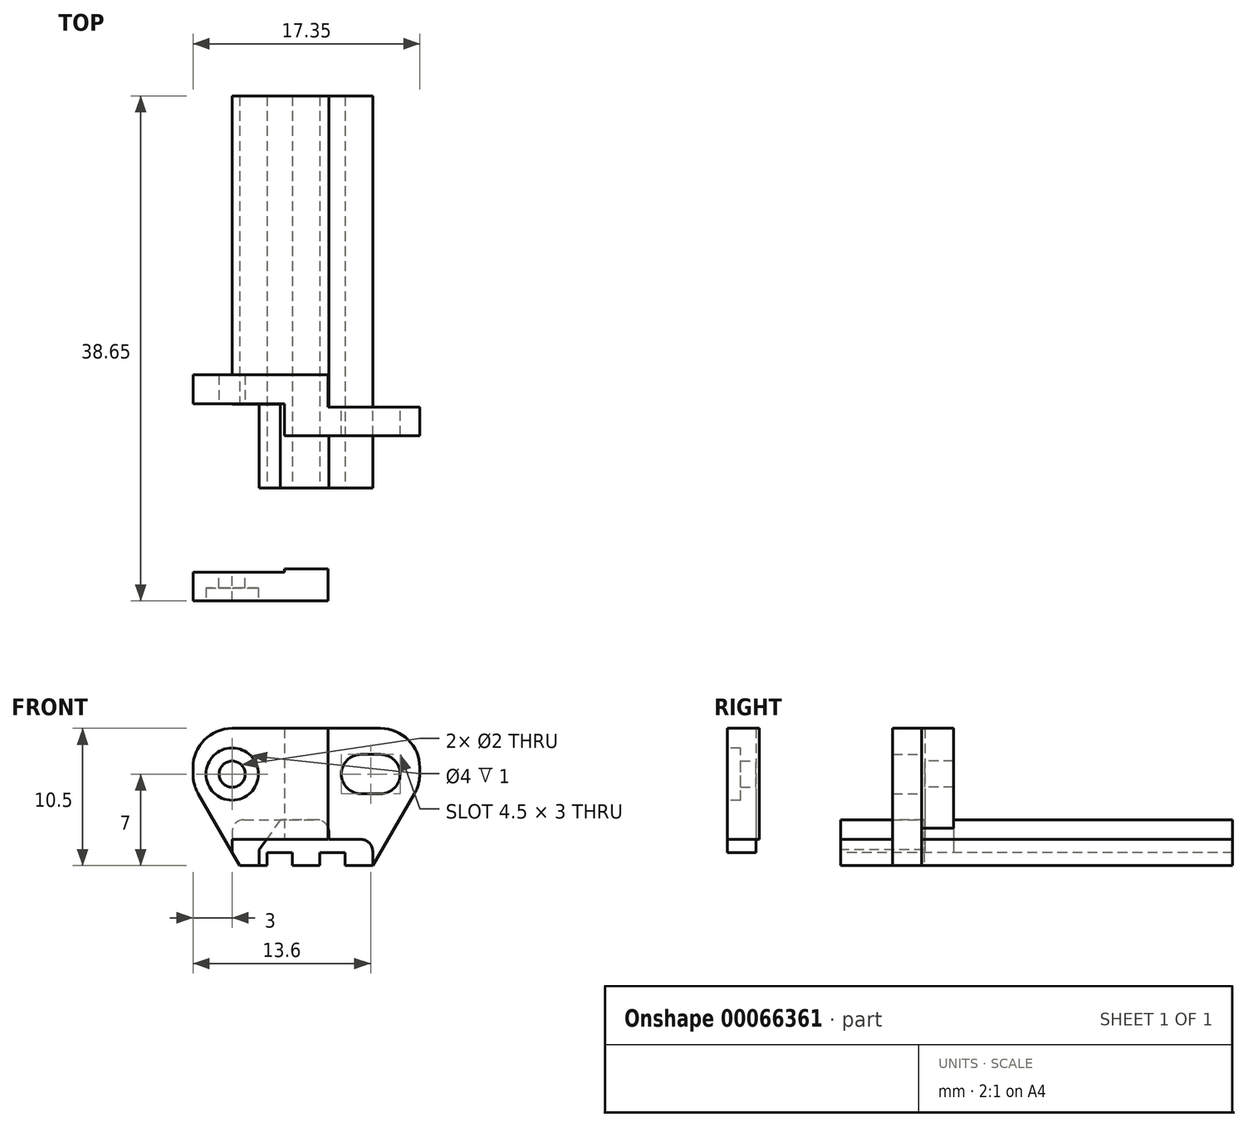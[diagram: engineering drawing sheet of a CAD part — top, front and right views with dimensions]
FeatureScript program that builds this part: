
annotation { "Feature Type Name" : "Feature", "Feature Type Description" : "" }
export const myFeature = defineFeature(function(context is Context, id is Id, definition is map)
    precondition{}
    {
        {
            var Q0;
            Q0=qCreatedBy(makeId("Front.planeOp"),FACE);
            var sketch = newSketch(context, id + "F0", { "sketchPlane" : qUnion([Q0])});
            skLineSegment(sketch, "E0", {"start": v(-8, 5) * mm, "end": v(24.45, 5) * mm, "construction": true});
            skArc(sketch, "E1", {"start": v(11.35, 3.5) * mm, "mid": v(12.85, 5) * mm, "end": v(11.35, 6.5) * mm});
            skArc(sketch, "E2", {"start": v(-3, 5) * mm, "mid": v(-2.65, 3.6) * mm, "end": v(-1.7, 2.52) * mm});
            skArc(sketch, "E3", {"start": v(14.35, 5) * mm, "mid": v(14, 3.6) * mm, "end": v(13.04, 2.52) * mm});
            skLineSegment(sketch, "E4", {"start": v(-1.7, 2.52) * mm, "end": v(2, 0) * mm});
            skLineSegment(sketch, "E5", {"start": v(13.04, 2.52) * mm, "end": v(9.35, 0) * mm});
            skLineSegment(sketch, "E6", {"start": v(4, 8.5) * mm, "end": v(4, 2) * mm});
            skLineSegment(sketch, "E7", {"start": v(9.35, 2) * mm, "end": v(7.35, 2) * mm});
            skLineSegment(sketch, "E8", {"start": v(4, 2) * mm, "end": v(2, 2) * mm});
            skLineSegment(sketch, "E9", {"start": v(4, 2) * mm, "end": v(7.35, 2) * mm});
            skLineSegment(sketch, "E10", {"start": v(7.35, 8.5) * mm, "end": v(7.35, 2) * mm});
            skLineSegment(sketch, "E11", {"start": v(2, 0) * mm, "end": v(9.35, 0) * mm});
            skLineSegment(sketch, "E12", {"start": v(2, 0) * mm, "end": v(2, 2) * mm});
            skLineSegment(sketch, "E13", {"start": v(9.35, 0) * mm, "end": v(9.35, 2) * mm});
            skLineSegment(sketch, "E14", {"start": v(0, 8.5) * mm, "end": v(11.35, 8.5) * mm});
            skLineSegment(sketch, "E15", {"start": v(-3, 5) * mm, "end": v(-3, 5.5) * mm});
            skLineSegment(sketch, "E16", {"start": v(14.35, 5) * mm, "end": v(14.35, 5.5) * mm});
            skPoint(sketch, "E16.endSnap0", {"position": v(14.35, 5) * mm});
            skPoint(sketch, "E17.visualSharp", {"position": v(-3, 8.5) * mm});
            skArc(sketch, "E17.filletArc", {"start": v(0, 8.5) * mm, "mid": v(-2.12, 7.62) * mm, "end": v(-3, 5.5) * mm});
            skPoint(sketch, "E18.visualSharp", {"position": v(14.35, 8.5) * mm});
            skArc(sketch, "E18.filletArc", {"start": v(14.35, 5.5) * mm, "mid": v(13.47, 7.62) * mm, "end": v(11.35, 8.5) * mm});
            skArc(sketch, "E19", {"start": v(9.85, 6.5) * mm, "mid": v(8.35, 5) * mm, "end": v(9.85, 3.5) * mm});
            skLineSegment(sketch, "E20", {"start": v(9.85, 6.5) * mm, "end": v(11.35, 6.5) * mm});
            skLineSegment(sketch, "E21", {"start": v(9.85, 3.5) * mm, "end": v(11.35, 3.5) * mm});
            skCircle(sketch, "E22", {"center": v(0, 5) * mm, "radius": 1 * mm});
            skSolve(sketch);
        }
        {
            var Q0;
            Q0=qCreatedBy(makeId("Front.planeOp"),FACE);
            var sketch = newSketch(context, id + "F1", { "sketchPlane" : qUnion([Q0])});
            skLineSegment(sketch, "E23.0", {"start": v(7.35, 8.5) * mm, "end": v(7.35, 2) * mm});
            skPoint(sketch, "E24.0.start.orphan", {"position": v(4, 2) * mm});
            skPoint(sketch, "E25.0.start.orphan", {"position": v(2, 0) * mm});
            skLineSegment(sketch, "E26.0", {"start": v(0, 8.5) * mm, "end": v(7.35, 8.5) * mm});
            skArc(sketch, "E27.0", {"start": v(0, 8.5) * mm, "mid": v(-2.12, 7.62) * mm, "end": v(-3, 5.5) * mm});
            skPoint(sketch, "E28.0", {"position": v(7.35, 0) * mm});
            skLineSegment(sketch, "E29.0", {"start": v(7.35, 2) * mm, "end": v(7.35, 0) * mm});
            skPoint(sketch, "E30.0.2.end.orphan", {"position": v(9.35, 2) * mm});
            skPoint(sketch, "E31.orphan", {"position": v(9.35, 0) * mm});
            skPoint(sketch, "E32.orphan", {"position": v(11.35, 8.5) * mm});
            skLineSegment(sketch, "E33", {"start": v(0, 0) * mm, "end": v(2, 0) * mm});
            skLineSegment(sketch, "E34", {"start": v(2, 0) * mm, "end": v(7.35, 0) * mm});
            skPoint(sketch, "E35.0.end.orphan", {"position": v(-3, 8.2) * mm});
            skLineSegment(sketch, "E36", {"start": v(-3, 4) * mm, "end": v(-3, 5.5) * mm});
            skArc(sketch, "E37.0", {"start": v(-3, 5) * mm, "mid": v(-2.9, 4.22) * mm, "end": v(-2.6, 3.5) * mm});
            skLineSegment(sketch, "E38", {"start": v(-2.6, 3.5) * mm, "end": v(-0.58, 0) * mm});
            skPoint(sketch, "E39.orphan", {"position": v(-1.7, 2.52) * mm});
            skLineSegment(sketch, "E40", {"start": v(0, 0) * mm, "end": v(0, -1) * mm});
            skLineSegment(sketch, "E41", {"start": v(0, -1) * mm, "end": v(-0.58, 0) * mm});
            skCircle(sketch, "E42.0", {"center": v(0, 5) * mm, "radius": 1 * mm});
            skSolve(sketch);
        }
        {
            var Q0;
            Q0=qSketchRegion(id+"F1",true);
            var Q1;
            Q1 = qSketchRegion(id + "F8", true);
            extrude(context, id + "F2", {"entities" : qUnion([Q0, Q1]), "oppositeDirection" : true, "depth" : 2.2 * mm});
        }
        {
            var Q0;
            Q0=qCreatedBy(makeId("Front.planeOp"),FACE);
            var sketch = newSketch(context, id + "F3", { "sketchPlane" : qUnion([Q0])});
            skLineSegment(sketch, "E43.0", {"start": v(4, 8.5) * mm, "end": v(4, 2) * mm});
            skLineSegment(sketch, "E44.0", {"start": v(7.35, 8.5) * mm, "end": v(7.35, 2) * mm});
            skLineSegment(sketch, "E45.0", {"start": v(4, 8.5) * mm, "end": v(7.35, 8.5) * mm});
            skLineSegment(sketch, "E46", {"start": v(7.35, 2) * mm, "end": v(7.35, 0) * mm});
            skLineSegment(sketch, "E47", {"start": v(7.35, 0) * mm, "end": v(4, 0) * mm});
            skLineSegment(sketch, "E48", {"start": v(4, 0) * mm, "end": v(4, 2) * mm});
            skPoint(sketch, "E49.0", {"position": v(7.35, 0) * mm});
            skPoint(sketch, "E50.0", {"position": v(4, 8.5) * mm});
            skPoint(sketch, "E51.0", {"position": v(7.35, 8.5) * mm});
            skPoint(sketch, "E52.0", {"position": v(4, 0) * mm});
            skSolve(sketch);
        }
        {
            var Q0;
            Q0=makeQuery(id+"F3.imprint","IMPRINT",FACE,{"disambiguationData":[TD([[makeQuery(id+"F3.imprint","IMPRINT",EDGE,{"derivedFrom":sQuery(id+"F3.wireOp",EDGE,"E43.0")}),1.0]])]});
            extrude(context, id + "F4", {"entities" : qUnion([Q0]), "operationType" : NewBodyOperationType.ADD, "depth" : .25 * mm});
        }
        {
            var Q0;
            Q0=makeQuery(id+"F4.opExtrude","CAP_FACE",FACE,{"disambiguationData":[OSD([sQuery(id+"F3.wireOp",EDGE,"E43.0"),sQuery(id+"F3.wireOp",EDGE,"E44.0"),sQuery(id+"F3.wireOp",EDGE,"E45.0"),sQuery(id+"F3.wireOp",EDGE,"E46"),sQuery(id+"F3.wireOp",EDGE,"E47"),sQuery(id+"F3.wireOp",EDGE,"E48")])],"isStart":false});
            var sketch = newSketch(context, id + "F5", { "sketchPlane" : qUnion([Q0])});
            skArc(sketch, "E53.0", {"start": v(14.35, 5) * mm, "mid": v(14.25, 4.22) * mm, "end": v(13.94, 3.5) * mm});
            skLineSegment(sketch, "E54", {"start": v(10.75, -1) * mm, "end": v(10.75, -2) * mm});
            skLineSegment(sketch, "E55", {"start": v(10.75, -2) * mm, "end": v(13.94, 3.5) * mm});
            skLineSegment(sketch, "E56.0", {"start": v(4, 8.5) * mm, "end": v(4, 2) * mm});
            skArc(sketch, "E57.0", {"start": v(14.35, 5.5) * mm, "mid": v(13.47, 7.62) * mm, "end": v(11.35, 8.5) * mm});
            skLineSegment(sketch, "E58.0", {"start": v(14.35, 5) * mm, "end": v(14.35, 5.5) * mm});
            skLineSegment(sketch, "E59", {"start": v(4, 2) * mm, "end": v(4, 0) * mm});
            skPoint(sketch, "E60.orphan", {"position": v(2, 0) * mm});
            skLineSegment(sketch, "E61.trimOffspring", {"start": v(4, 8.5) * mm, "end": v(11.35, 8.5) * mm});
            skPoint(sketch, "E62.0.start.orphan", {"position": v(0, 8.5) * mm});
            skLineSegment(sketch, "E63", {"start": v(7.39, 0) * mm, "end": v(10.75, -1) * mm});
            skLineSegment(sketch, "E64", {"start": v(4, 0) * mm, "end": v(7.39, 0) * mm});
            skLineSegment(sketch, "E65.0", {"start": v(9.85, 3.5) * mm, "end": v(11.35, 3.5) * mm});
            skArc(sketch, "E66.0", {"start": v(9.85, 6.5) * mm, "mid": v(8.35, 5) * mm, "end": v(9.85, 3.5) * mm});
            skLineSegment(sketch, "E67.0", {"start": v(9.85, 6.5) * mm, "end": v(11.35, 6.5) * mm});
            skArc(sketch, "E68.0", {"start": v(11.35, 3.5) * mm, "mid": v(12.85, 5) * mm, "end": v(11.35, 6.5) * mm});
            skSolve(sketch);
        }
        {
            var Q0;
            Q0=qSketchRegion(id+"F5",true);
            extrude(context, id + "F6", {"entities" : qUnion([Q0]), "depth" : 2.2 * mm});
        }
        {
            var Q0;
            Q0=makeQuery(id+"F6.opExtrude","CAP_FACE",FACE,{"disambiguationData":[OSD([sQuery(id+"F5.wireOp",EDGE,"E53.0"),sQuery(id+"F5.wireOp",EDGE,"234c2655-9adb-407f-9d6a-58d03281b655.0"),sQuery(id+"F5.wireOp",EDGE,"E54"),sQuery(id+"F5.wireOp",EDGE,"E55"),sQuery(id+"F5.wireOp",EDGE,"E56.0"),sQuery(id+"F5.wireOp",EDGE,"E57.0"),sQuery(id+"F5.wireOp",EDGE,"E58.0"),sQuery(id+"F5.wireOp",EDGE,"E59"),sQuery(id+"F5.wireOp",EDGE,"E61.trimOffspring"),sQuery(id+"F5.wireOp",EDGE,"E63"),sQuery(id+"F5.wireOp",EDGE,"E64")])],"isStart":false});
            cPlane(context, id + "F7", {"entities" : qUnion([Q0]), "cplaneType" : CPlaneType.OFFSET, "offset" : 4 * mm, "width" : 150 * mm, "height" : 150 * mm});
        }
        {
            var Q0;
            Q0=qCreatedBy(id+"F7.planeOp",FACE);
            var sketch = newSketch(context, id + "F8", { "sketchPlane" : qUnion([Q0])});
            skLineSegment(sketch, "E69.0", {"start": v(10.75, -2) * mm, "end": v(13.94, 3.5) * mm});
            skLineSegment(sketch, "E70.0", {"start": v(10.75, -1) * mm, "end": v(10.75, -2) * mm});
            skLineSegment(sketch, "E71", {"start": v(7.39, 0) * mm, "end": v(7.39, 0) * mm});
            skLineSegment(sketch, "E72", {"start": v(7.39, 0) * mm, "end": v(7.39, 0.6) * mm});
            skLineSegment(sketch, "E73", {"start": v(6.49, 1.5) * mm, "end": v(0.9, 1.5) * mm});
            skLineSegment(sketch, "E74", {"start": v(10.75, -2) * mm, "end": v(8.65, -2) * mm});
            skLineSegment(sketch, "E75", {"start": v(8.65, -2) * mm, "end": v(8.65, -1) * mm});
            skLineSegment(sketch, "E76", {"start": v(8.65, -1) * mm, "end": v(6.71, -1) * mm});
            skLineSegment(sketch, "E77", {"start": v(6.71, -1) * mm, "end": v(6.71, -2) * mm});
            skLineSegment(sketch, "E78", {"start": v(6.71, -2) * mm, "end": v(4.61, -2) * mm});
            skLineSegment(sketch, "E79", {"start": v(4.61, -2) * mm, "end": v(4.61, -1) * mm});
            skLineSegment(sketch, "E80", {"start": v(4.61, -1) * mm, "end": v(2.68, -1) * mm});
            skLineSegment(sketch, "E81", {"start": v(2.68, -1) * mm, "end": v(2.68, -2) * mm});
            skLineSegment(sketch, "E82", {"start": v(0, -1) * mm, "end": v(0, 0.6) * mm});
            skPoint(sketch, "E83.orphan", {"position": v(-2.6, 3.5) * mm});
            skPoint(sketch, "E84.orphan", {"position": v(0, -1) * mm});
            skLineSegment(sketch, "E85", {"start": v(0, -1) * mm, "end": v(0.58, -2) * mm});
            skLineSegment(sketch, "E86", {"start": v(2.68, -2) * mm, "end": v(0.58, -2) * mm});
            skLineSegment(sketch, "E87", {"start": v(7.39, 0) * mm, "end": v(9.85, 0) * mm});
            skLineSegment(sketch, "E88", {"start": v(10.75, -1) * mm, "end": v(10.75, -0.9) * mm});
            skPoint(sketch, "E89.visualSharp", {"position": v(10.75, 0) * mm});
            skArc(sketch, "E89.filletArc", {"start": v(10.75, -0.9) * mm, "mid": v(10.49, -0.26) * mm, "end": v(9.85, 0) * mm});
            skPoint(sketch, "E90.visualSharp", {"position": v(0, 1.5) * mm});
            skArc(sketch, "E90.filletArc", {"start": v(0.9, 1.5) * mm, "mid": v(0.26, 1.24) * mm, "end": v(0, 0.6) * mm});
            skPoint(sketch, "E91.visualSharp", {"position": v(7.39, 1.5) * mm});
            skArc(sketch, "E91.filletArc", {"start": v(7.39, 0.6) * mm, "mid": v(7.13, 1.24) * mm, "end": v(6.49, 1.5) * mm});
            skSolve(sketch);
        }
        {
            var Q0;
            Q0 = qSketchRegion(id + "F8", true);
            extrude(context, id + "F9", {"entities" : qUnion([Q0]), "oppositeDirection" : true, "depth" : 30 * mm});
        }
        {
            var Q0;
            Q0=qCreatedBy(id+"F7.planeOp",FACE);
            var sketch = newSketch(context, id + "F10", { "sketchPlane" : qUnion([Q0])});
            skLineSegment(sketch, "E92", {"start": v(0, 0.6) * mm, "end": v(0, -1) * mm});
            skPoint(sketch, "E93.orphan", {"position": v(6.49, 1.5) * mm});
            skPoint(sketch, "E94.orphan", {"position": v(4, 2) * mm});
            skLineSegment(sketch, "E95.0", {"start": v(2.08, -2) * mm, "end": v(0.58, -2) * mm});
            skArc(sketch, "E96.0", {"start": v(0.9, 1.5) * mm, "mid": v(0.26, 1.24) * mm, "end": v(0, 0.6) * mm});
            skLineSegment(sketch, "E97.0", {"start": v(0, -1) * mm, "end": v(0.58, -2) * mm});
            skLineSegment(sketch, "E98", {"start": v(0.9, 1.5) * mm, "end": v(3.68, 1.5) * mm});
            skLineSegment(sketch, "E99", {"start": v(3.68, 1.5) * mm, "end": v(2.08, -0.8) * mm});
            skLineSegment(sketch, "E100", {"start": v(2.08, -0.8) * mm, "end": v(2.08, -2) * mm});
            skPoint(sketch, "E101.0", {"position": v(2.68, -2) * mm});
            skSolve(sketch);
        }
        {
            var Q0;
            Q0 = qSketchRegion(id + "F10", true);
            extrude(context, id + "F11", {"entities" : qUnion([Q0]), "operationType" : NewBodyOperationType.REMOVE, "oppositeDirection" : true, "depth" : 6.4 * mm});
        }
        {
            var Q0;
            Q0=makeQuery(id+"F2.opExtrude","SWEPT_BODY",BODY,{"disambiguationData":[OSD([sQuery(id+"F1.wireOp",EDGE,"E23.0"),sQuery(id+"F1.wireOp",EDGE,"E26.0"),sQuery(id+"F1.wireOp",EDGE,"E27.0"),sQuery(id+"F1.wireOp",EDGE,"E29.0"),sQuery(id+"F1.wireOp",EDGE,"8a8849a1-0ef2-4d3a-a45b-3f32d24ec19d.0"),sQuery(id+"F1.wireOp",EDGE,"a5861810-6e58-4b75-8f57-02ec5fb935cc.0"),sQuery(id+"F1.wireOp",EDGE,"b8a016af-5f0e-415b-8942-6e5b113ceea2.0"),sQuery(id+"F1.wireOp",EDGE,"5ff575cd-ac4e-4935-8ca6-a719c286e6e0.0"),sQuery(id+"F1.wireOp",EDGE,"E33"),sQuery(id+"F1.wireOp",EDGE,"E34"),sQuery(id+"F1.wireOp",EDGE,"E36"),sQuery(id+"F1.wireOp",EDGE,"E37.0"),sQuery(id+"F1.wireOp",EDGE,"E38"),sQuery(id+"F1.wireOp",EDGE,"E40"),sQuery(id+"F1.wireOp",EDGE,"E41")])]});
            var Q1;
            Q1=qCreatedBy(id+"F7.planeOp",FACE);
            mirror(context, id + "F12", {"operationType" : NewBodyOperationType.ADD, "entities" : qUnion([Q0]), "mirrorPlane" : qUnion([Q1])});
        }
        {
            var Q0;
            Q0=makeQuery(id+"F12.opPattern","COPY",FACE,{"derivedFrom":makeQuery(id+"F2.opExtrude","CAP_FACE",FACE,{"disambiguationData":[OSD([sQuery(id+"F1.wireOp",EDGE,"E23.0"),sQuery(id+"F1.wireOp",EDGE,"E26.0"),sQuery(id+"F1.wireOp",EDGE,"E27.0"),sQuery(id+"F1.wireOp",EDGE,"E29.0"),sQuery(id+"F1.wireOp",EDGE,"E33"),sQuery(id+"F1.wireOp",EDGE,"E34"),sQuery(id+"F1.wireOp",EDGE,"E36"),sQuery(id+"F1.wireOp",EDGE,"E37.0"),sQuery(id+"F1.wireOp",EDGE,"E38"),sQuery(id+"F1.wireOp",EDGE,"E40"),sQuery(id+"F1.wireOp",EDGE,"E41"),sQuery(id+"F1.wireOp",EDGE,"E42.0")])],"isStart":false}),"instanceName":"1"});
            var sketch = newSketch(context, id + "F13", { "sketchPlane" : qUnion([Q0])});
            skCircle(sketch, "E102", {"center": v(0, 5) * mm, "radius": 2 * mm});
            skSolve(sketch);
        }
        {
            var Q0;
            Q0=makeQuery(id+"F13.imprint","IMPRINT",FACE,{"disambiguationData":[TD([[makeQuery(id+"F13.imprint","IMPRINT",EDGE,{"derivedFrom":sQuery(id+"F13.wireOp",EDGE,"E102")}),1.0]])]});
            extrude(context, id + "F14", {"entities" : qUnion([Q0]), "operationType" : NewBodyOperationType.REMOVE, "oppositeDirection" : true, "depth" : 1 * mm});
        }
    });
